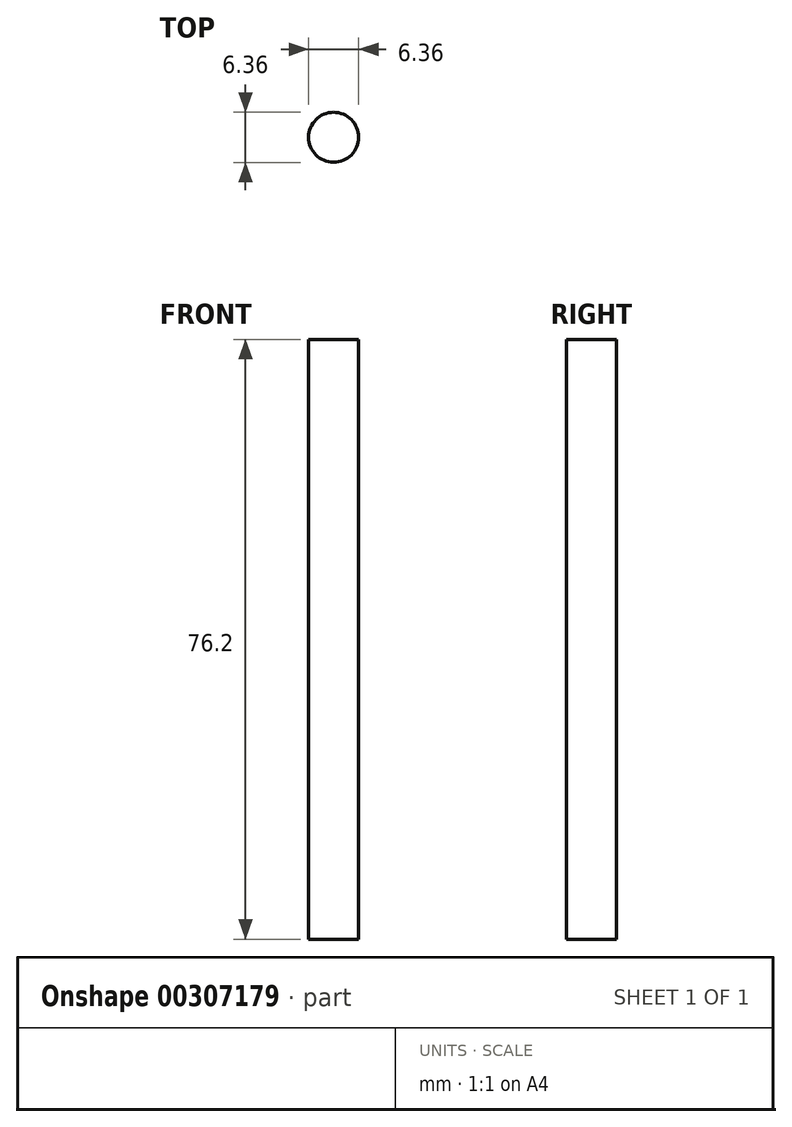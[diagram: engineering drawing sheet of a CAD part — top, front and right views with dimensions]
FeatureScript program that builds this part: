
annotation { "Feature Type Name" : "Feature", "Feature Type Description" : "" }
export const myFeature = defineFeature(function(context is Context, id is Id, definition is map)
    precondition{}
    {
        {
            var Q0;
            Q0=qCreatedBy(makeId("Top.planeOp"),FACE);
            var sketch = newSketch(context, id + "F0", { "sketchPlane" : qUnion([Q0])});
            skCircle(sketch, "E0", {"center": v(0, 0) * mm, "radius": 3.18 * mm});
            skSolve(sketch);
        }
        {
            var Q0;
            Q0=makeQuery(id+"F0.imprint","IMPRINT",FACE,{"disambiguationData":[TD([[makeQuery(id+"F0.imprint","IMPRINT",EDGE,{"derivedFrom":sQuery(id+"F0.wireOp",EDGE,"E0")}),1.0]])]});
            extrude(context, id + "F1", {"entities" : qUnion([Q0]), "depth" : 76.2 * mm});
        }
        {
            var Q0;
            Q0=makeQuery(id+"F1.opExtrude","CAP_FACE",FACE,{"disambiguationData":[OSD([sQuery(id+"F0.wireOp",EDGE,"E0")])],"isStart":false});
            extrude(context, id + "F2", {"entities" : qUnion([Q0]), "operationType" : NewBodyOperationType.REMOVE, "oppositeDirection" : true, "depth" : 25.4 * mm});
        }
        {
            var Q0;
            Q0=makeQuery(id+"F2.boolean.opBoolean","COPY",FACE,{"derivedFrom":makeQuery(id+"F2.opExtrude","CAP_FACE",FACE,{"disambiguationData":[OSD([sQuery(id+"F0.wireOp",EDGE,"E0")])],"isStart":false})});
            extrude(context, id + "F3", {"entities" : qUnion([Q0]), "operationType" : NewBodyOperationType.ADD, "depth" : 25.4 * mm});
        }
    });
